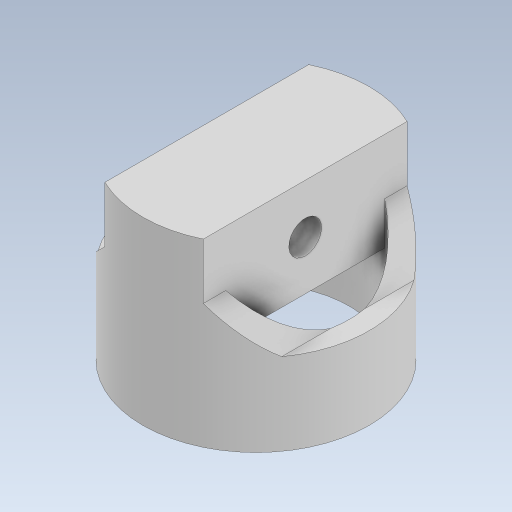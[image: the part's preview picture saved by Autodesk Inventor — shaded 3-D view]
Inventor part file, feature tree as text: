
AUTODESK INVENTOR PART (.ipt)
format: ipt  version: 2024 (Build 280153000, 153)  size: 255,488 bytes
history: native  units: mm
features: extrude x3, other x1, chamfer x1, sketch x1, projected_geometry x1
ambient origin geometry x8: Origin, YZ Plane, XZ Plane, XY Plane, X Axis, Y Axis, Z Axis, Center Point
bodies: Body1 (feature_tree)
feature tree (7):
  other  "솔리드1"
  extrude  "돌출1"  Depth=5.7mm
  extrude  "돌출2"  Depth=6.9mm
  chamfer  "모따기3"  Distance=2.5mm
  extrude  "돌출5"  Depth=3.0mm
  sketch  "스케치6"
  projected_geometry  "투영된 루프4"
